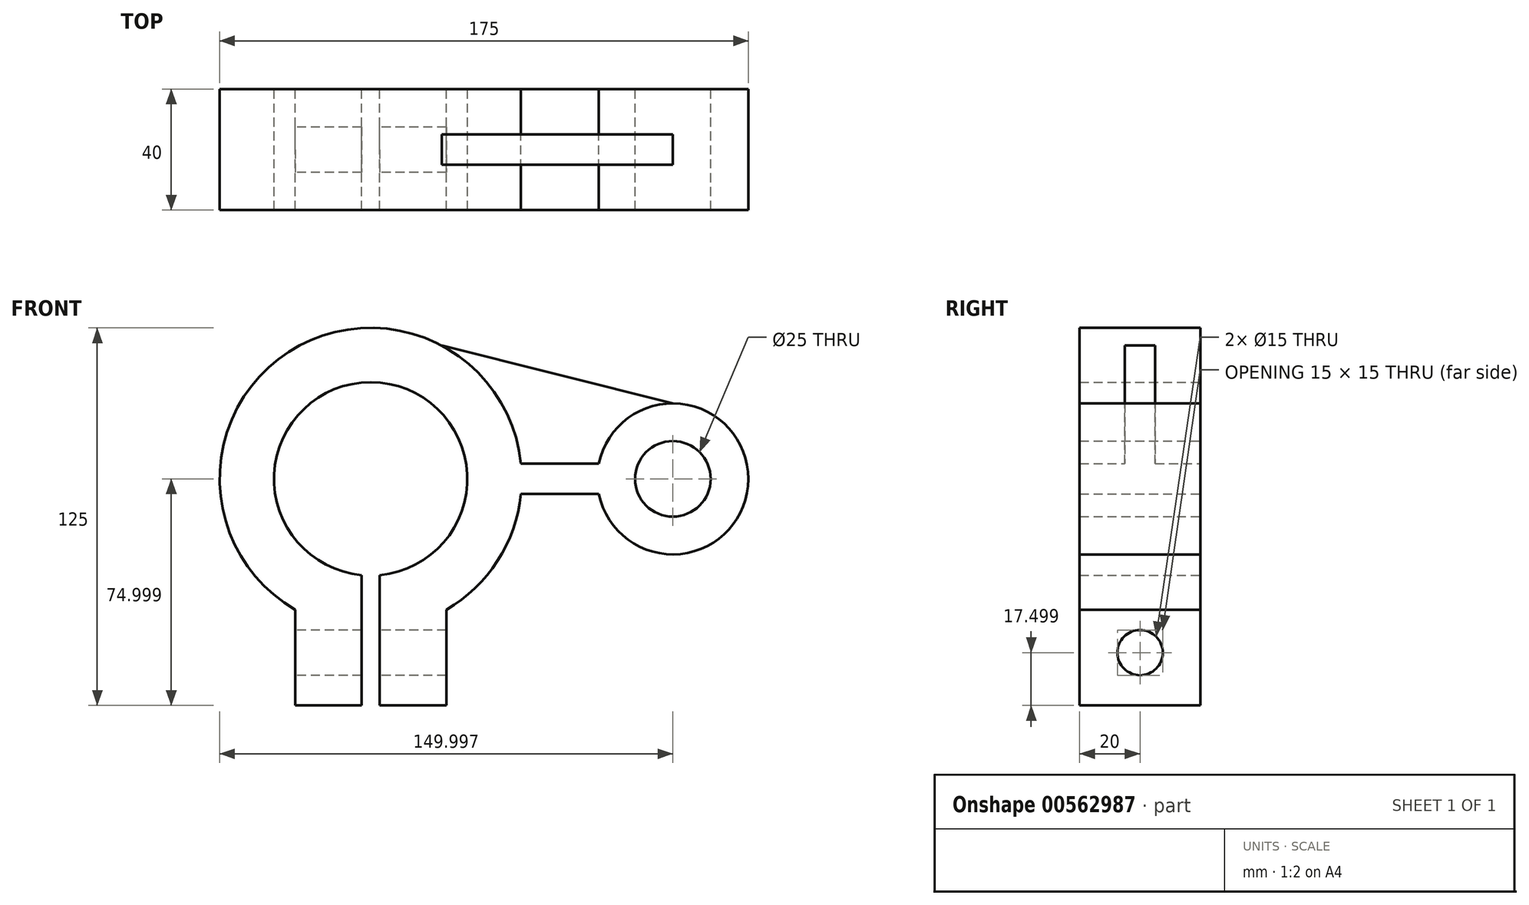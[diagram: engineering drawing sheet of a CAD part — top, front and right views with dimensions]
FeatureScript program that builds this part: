
annotation { "Feature Type Name" : "Feature", "Feature Type Description" : "" }
export const myFeature = defineFeature(function(context is Context, id is Id, definition is map)
    precondition{}
    {
        {
            var Q0;
            Q0=qCreatedBy(makeId("Front.planeOp"),FACE);
            var sketch = newSketch(context, id + "F0", { "sketchPlane" : qUnion([Q0])});
            skArc(sketch, "E0", {"start": v(37.48, 3.89) * mm, "mid": v(-39.4, 40.88) * mm, "end": v(-37.27, -44.41) * mm});
            skArc(sketch, "E1", {"start": v(-9.27, -32.97) * mm, "mid": v(-12.27, 30.89) * mm, "end": v(-15.27, -32.97) * mm});
            skArc(sketch, "E2", {"start": v(63.23, -6.11) * mm, "mid": v(112.73, -1.11) * mm, "end": v(63.23, 3.89) * mm});
            skCircle(sketch, "E3", {"center": v(87.73, -1.11) * mm, "radius": 12.5 * mm});
            skLineSegment(sketch, "E4.bottom", {"start": v(37.48, 3.89) * mm, "end": v(63.23, 3.89) * mm});
            skLineSegment(sketch, "E4.top", {"start": v(37.48, -6.11) * mm, "end": v(63.23, -6.11) * mm});
            skLineSegment(sketch, "E5", {"start": v(11.26, 43) * mm, "end": v(87.73, 23.89) * mm});
            skLineSegment(sketch, "E6.left", {"start": v(-9.27, -33.11) * mm, "end": v(-9.27, -76.11) * mm});
            skLineSegment(sketch, "E7.top", {"start": v(-37.27, -76.11) * mm, "end": v(-15.27, -76.11) * mm});
            skLineSegment(sketch, "E7.left", {"start": v(-37.27, -44.41) * mm, "end": v(-37.27, -76.11) * mm});
            skLineSegment(sketch, "E8", {"start": v(12.73, -76.11) * mm, "end": v(12.73, -44.41) * mm});
            skArc(sketch, "E9.trimOffspring", {"start": v(12.73, -44.41) * mm, "mid": v(29.72, -28.25) * mm, "end": v(37.48, -6.11) * mm});
            skLineSegment(sketch, "E10", {"start": v(-15.27, -76.11) * mm, "end": v(-15.27, -32.97) * mm});
            skLineSegment(sketch, "E11", {"start": v(-9.27, -32.97) * mm, "end": v(-9.27, -33.11) * mm});
            skLineSegment(sketch, "E12.trimOffspring", {"start": v(-9.27, -76.11) * mm, "end": v(12.73, -76.11) * mm});
            skPoint(sketch, "E13.orphan", {"position": v(-12.27, 48.89) * mm});
            skSolve(sketch);
        }
        {
            var Q0;
            Q0=makeQuery(id+"F0.imprint","IMPRINT",FACE,{"disambiguationData":[TD([[makeQuery(id+"F0.imprint","IMPRINT",EDGE,{"derivedFrom":sQuery(id+"F0.wireOp",EDGE,"E1")}),-1.0]])]});
            extrude(context, id + "F1", {"entities" : qUnion([Q0]), "endBound" : BoundingType.SYMMETRIC, "depth" : 40 * mm, "offsetDistance" : 25.4 * mm});
        }
        {
            var Q0;
            {var subQ0=sQuery(id+"F0.wireOp",EDGE,"E4.bottom");Q0=makeQuery(id+"F0.imprint","IMPRINT",FACE,{"disambiguationData":[TD([[makeQuery(id+"F0.imprint","IMPRINT",EDGE,{"derivedFrom":subQ0}),1.0]])]});}
            extrude(context, id + "F2", {"entities" : qUnion([Q0]), "operationType" : NewBodyOperationType.ADD, "endBound" : BoundingType.SYMMETRIC, "depth" : 10 * mm, "offsetDistance" : 25.4 * mm});
        }
        {
            var Q0;
            Q0=qCreatedBy(makeId("Right.planeOp"),FACE);
            var sketch = newSketch(context, id + "F3", { "sketchPlane" : qUnion([Q0])});
            skCircle(sketch, "E14", {"center": v(0, -58.61) * mm, "radius": 7.5 * mm});
            skPoint(sketch, "E15.orphan", {"position": v(0, -51.11) * mm});
            skPoint(sketch, "E16.end.orphan", {"position": v(0, -66.11) * mm});
            skSolve(sketch);
        }
        {
            var Q0;
            Q0 = qSketchRegion(id + "F3", true);
            extrude(context, id + "F4", {"entities" : qUnion([Q0]), "operationType" : NewBodyOperationType.REMOVE, "endBound" : BoundingType.SYMMETRIC, "depth" : 100 * mm, "offsetDistance" : 25.4 * mm});
        }
    });
